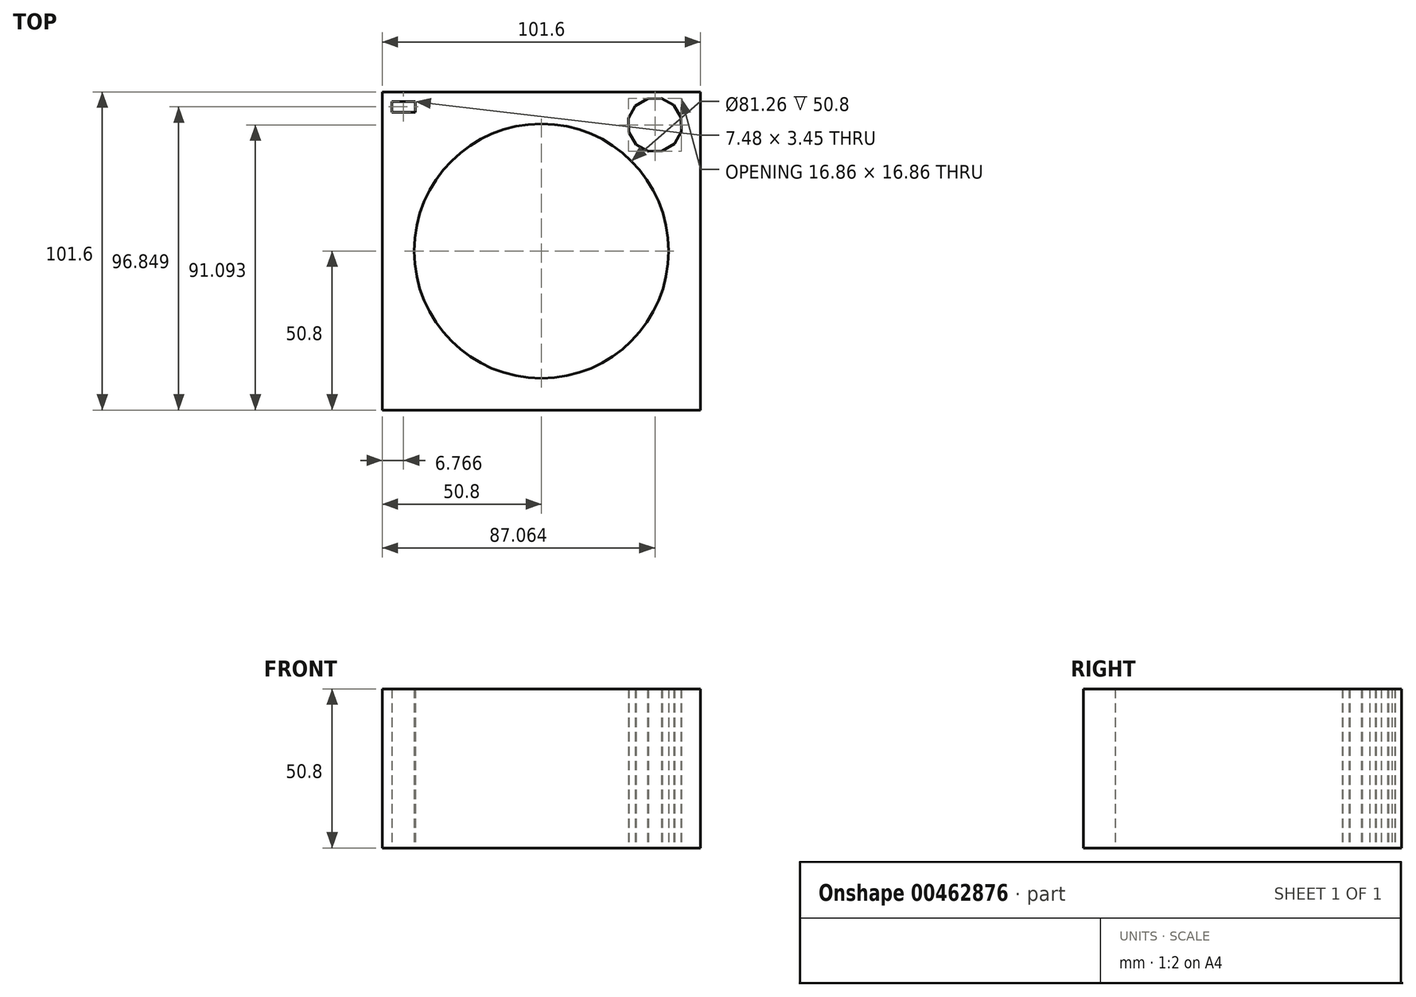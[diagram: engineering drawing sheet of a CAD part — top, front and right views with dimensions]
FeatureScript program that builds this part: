
annotation { "Feature Type Name" : "Feature", "Feature Type Description" : "" }
export const myFeature = defineFeature(function(context is Context, id is Id, definition is map)
    precondition{}
    {
        {
            var Q0;
            Q0=qCreatedBy(makeId("Top.planeOp"),FACE);
            var sketch = newSketch(context, id + "F0", { "sketchPlane" : qUnion([Q0])});
            skLineSegment(sketch, "E0.bottom", {"start": v(50.8, 50.8) * mm, "end": v(-50.8, 50.8) * mm});
            skLineSegment(sketch, "E0.top", {"start": v(50.8, -50.8) * mm, "end": v(-50.8, -50.8) * mm});
            skLineSegment(sketch, "E0.left", {"start": v(50.8, 50.8) * mm, "end": v(50.8, -50.8) * mm});
            skLineSegment(sketch, "E0.right", {"start": v(-50.8, 50.8) * mm, "end": v(-50.8, -50.8) * mm});
            skPoint(sketch, "E0.middle", {"position": v(0, 0) * mm});
            skCircle(sketch, "E1", {"center": v(0, 0) * mm, "radius": 40.63 * mm});
            skCircle(sketch, "E2.cCircle", {"center": v(36.26, 40.3) * mm, "radius": 8.4 * mm, "construction": true});
            skLineSegment(sketch, "E2.0", {"start": v(42.3, 46.54) * mm, "end": v(44.62, 42.68) * mm});
            skLineSegment(sketch, "E2.1", {"start": v(44.62, 42.68) * mm, "end": v(44.7, 38.19) * mm});
            skLineSegment(sketch, "E2.2", {"start": v(44.7, 38.19) * mm, "end": v(42.5, 34.25) * mm});
            skLineSegment(sketch, "E2.3", {"start": v(42.5, 34.25) * mm, "end": v(38.65, 31.94) * mm});
            skLineSegment(sketch, "E2.4", {"start": v(38.65, 31.94) * mm, "end": v(34.16, 31.87) * mm});
            skLineSegment(sketch, "E2.5", {"start": v(34.16, 31.87) * mm, "end": v(30.23, 34.05) * mm});
            skLineSegment(sketch, "E2.6", {"start": v(30.23, 34.05) * mm, "end": v(27.91, 37.9) * mm});
            skLineSegment(sketch, "E2.7", {"start": v(27.91, 37.9) * mm, "end": v(27.84, 42.4) * mm});
            skLineSegment(sketch, "E2.8", {"start": v(27.84, 42.4) * mm, "end": v(30.02, 46.33) * mm});
            skLineSegment(sketch, "E2.9", {"start": v(30.02, 46.33) * mm, "end": v(33.87, 48.64) * mm});
            skLineSegment(sketch, "E2.10", {"start": v(33.87, 48.64) * mm, "end": v(38.37, 48.72) * mm});
            skLineSegment(sketch, "E2.11", {"start": v(38.37, 48.72) * mm, "end": v(42.3, 46.54) * mm});
            skPoint(sketch, "E2.0.midPoint", {"position": v(43.46, 44.6) * mm});
            skLineSegment(sketch, "E3.bottom", {"start": v(-40.3, 44.32) * mm, "end": v(-47.78, 44.32) * mm});
            skLineSegment(sketch, "E3.top", {"start": v(-40.3, 47.78) * mm, "end": v(-47.78, 47.78) * mm});
            skLineSegment(sketch, "E3.left", {"start": v(-40.3, 44.32) * mm, "end": v(-40.3, 47.78) * mm});
            skLineSegment(sketch, "E3.right", {"start": v(-47.78, 44.32) * mm, "end": v(-47.78, 47.78) * mm});
            skPoint(sketch, "E3.middle", {"position": v(-44.03, 46.05) * mm});
            skSolve(sketch);
        }
        {
            var Q0;
            Q0=makeQuery(id+"F0.imprint","IMPRINT",FACE,{"disambiguationData":[TD([[makeQuery(id+"F0.imprint","IMPRINT",EDGE,{"derivedFrom":sQuery(id+"F0.wireOp",EDGE,"E0.bottom")}),1.0]])]});
            extrude(context, id + "F1", {"entities" : qUnion([Q0]), "depth" : 50.8 * mm});
        }
        {
            var Q0;
            Q0=makeQuery(id+"F1.opExtrude","CAP_FACE",FACE,{"disambiguationData":[OSD([sQuery(id+"F0.wireOp",EDGE,"E0.bottom"),sQuery(id+"F0.wireOp",EDGE,"E0.top"),sQuery(id+"F0.wireOp",EDGE,"E0.left"),sQuery(id+"F0.wireOp",EDGE,"E0.right"),sQuery(id+"F0.wireOp",EDGE,"E1"),sQuery(id+"F0.wireOp",EDGE,"E2.0"),sQuery(id+"F0.wireOp",EDGE,"E2.1"),sQuery(id+"F0.wireOp",EDGE,"E2.2"),sQuery(id+"F0.wireOp",EDGE,"E2.3"),sQuery(id+"F0.wireOp",EDGE,"E2.4"),sQuery(id+"F0.wireOp",EDGE,"E2.5"),sQuery(id+"F0.wireOp",EDGE,"E2.6"),sQuery(id+"F0.wireOp",EDGE,"E2.7"),sQuery(id+"F0.wireOp",EDGE,"E2.8"),sQuery(id+"F0.wireOp",EDGE,"E2.9"),sQuery(id+"F0.wireOp",EDGE,"E2.10"),sQuery(id+"F0.wireOp",EDGE,"E2.11"),sQuery(id+"F0.wireOp",EDGE,"E3.bottom"),sQuery(id+"F0.wireOp",EDGE,"E3.top"),sQuery(id+"F0.wireOp",EDGE,"E3.left"),sQuery(id+"F0.wireOp",EDGE,"E3.right")])],"isStart":false});
            var sketch = newSketch(context, id + "F2", { "sketchPlane" : qUnion([Q0])});
            skCircle(sketch, "E4", {"center": v(-37, 36.54) * mm, "radius": 7.02 * mm});
            skSolve(sketch);
        }
        {
            var Q0;
            Q0=makeQuery(id+"F2.imprint","IMPRINT",FACE,{"disambiguationData":[TD([[makeQuery(id+"F2.imprint","IMPRINT",EDGE,{"derivedFrom":sQuery(id+"F2.wireOp",EDGE,"E4")}),1.0]])]});
            extrude(context, id + "F3", {"entities" : qUnion([Q0]), "operationType" : NewBodyOperationType.ADD, "depth" : -25.4 * mm});
        }
    });
